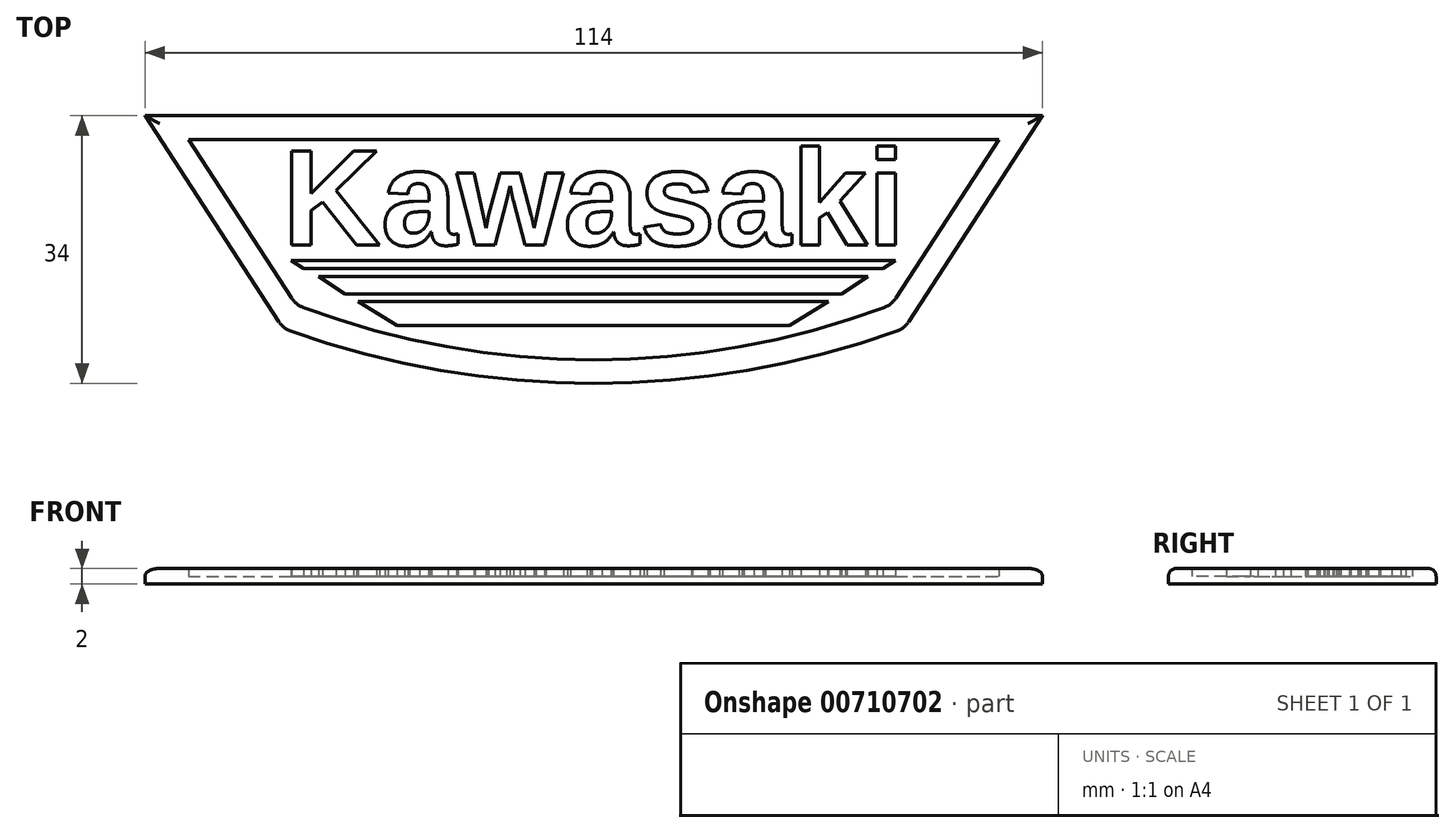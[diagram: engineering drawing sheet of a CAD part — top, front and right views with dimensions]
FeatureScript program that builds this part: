
annotation { "Feature Type Name" : "Feature", "Feature Type Description" : "" }
export const myFeature = defineFeature(function(context is Context, id is Id, definition is map)
    precondition{}
    {
        {
            var Q0;
            Q0=qCreatedBy(makeId("Top.planeOp"),FACE);
            var sketch = newSketch(context, id + "F0", { "sketchPlane" : qUnion([Q0])});
            skLineSegment(sketch, "E0.bottom", {"start": v(57, -17) * mm, "end": v(-57, -17) * mm});
            skLineSegment(sketch, "E0.top", {"start": v(57, 17) * mm, "end": v(-57, 17) * mm});
            skLineSegment(sketch, "E0.left", {"start": v(57, -17) * mm, "end": v(57, 17) * mm});
            skLineSegment(sketch, "E0.right", {"start": v(-57, -17) * mm, "end": v(-57, 17) * mm});
            skPoint(sketch, "E0.middle", {"position": v(0, 0) * mm});
            skLineSegment(sketch, "E1.top", {"start": v(57, -10) * mm, "end": v(-57, -10) * mm});
            skLineSegment(sketch, "E1.right", {"start": v(-57, 17) * mm, "end": v(-57, -10) * mm});
            skLineSegment(sketch, "E2", {"start": v(-57, 17) * mm, "end": v(-40.01, -9.15) * mm});
            skLineSegment(sketch, "E3", {"start": v(57, 17) * mm, "end": v(40.01, -9.15) * mm});
            skArc(sketch, "E4", {"start": v(-38.5, -10.35) * mm, "mid": v(0, -17) * mm, "end": v(38.5, -10.35) * mm});
            skLineSegment(sketch, "E5", {"start": v(-51.47, 14) * mm, "end": v(51.47, 14) * mm});
            skLineSegment(sketch, "E6", {"start": v(-51.47, 14) * mm, "end": v(-38.37, -6.18) * mm});
            skLineSegment(sketch, "E7", {"start": v(38.37, -6.18) * mm, "end": v(51.47, 14) * mm});
            skArc(sketch, "E8", {"start": v(-36.9, -7.35) * mm, "mid": v(0, -14) * mm, "end": v(36.9, -7.35) * mm});
            skPoint(sketch, "E9.visualSharp", {"position": v(-39.47, -10) * mm});
            skArc(sketch, "E9.filletArc", {"start": v(-40.01, -9.15) * mm, "mid": v(-39.36, -9.88) * mm, "end": v(-38.5, -10.35) * mm});
            skPoint(sketch, "E10.visualSharp", {"position": v(-37.84, -7) * mm});
            skArc(sketch, "E10.filletArc", {"start": v(-38.37, -6.18) * mm, "mid": v(-37.73, -6.88) * mm, "end": v(-36.9, -7.35) * mm});
            skPoint(sketch, "E11.visualSharp", {"position": v(37.84, -7) * mm});
            skArc(sketch, "E11.filletArc", {"start": v(36.9, -7.35) * mm, "mid": v(37.73, -6.88) * mm, "end": v(38.37, -6.18) * mm});
            skPoint(sketch, "E12.visualSharp", {"position": v(39.47, -10) * mm});
            skArc(sketch, "E12.filletArc", {"start": v(38.5, -10.35) * mm, "mid": v(39.36, -9.88) * mm, "end": v(40.01, -9.15) * mm});
            skSolve(sketch);
        }
        {
            var Q0;
            Q0=makeQuery(id+"F0.imprint","IMPRINT",FACE,{"disambiguationData":[TD([[makeQuery(id+"F0.imprint","IMPRINT",EDGE,{"derivedFrom":sQuery(id+"F0.wireOp",EDGE,"E5")}),-1.0]])]});
            var sketch = newSketch(context, id + "F1", { "sketchPlane" : qUnion([Q0])});
            skText(sketch, "E13", { "text": "Kawasaki", "fontName": "Arimo-Bold.ttf"});
            skLineSegment(sketch, "E14.bottom", {"start": v(-38.48, -1.42) * mm, "end": v(38.36, -1.42) * mm});
            skLineSegment(sketch, "E14.top", {"start": v(-38.48, -2.42) * mm, "end": v(38.36, -2.42) * mm});
            skLineSegment(sketch, "E14.left", {"start": v(-38.48, -1.42) * mm, "end": v(-38.48, -2.42) * mm});
            skLineSegment(sketch, "E14.right", {"start": v(38.36, -1.42) * mm, "end": v(38.36, -2.42) * mm});
            skLineSegment(sketch, "E15.bottom", {"start": v(-34.98, -3.42) * mm, "end": v(34.86, -3.42) * mm});
            skLineSegment(sketch, "E15.top", {"start": v(-34.98, -5.62) * mm, "end": v(34.86, -5.62) * mm});
            skLineSegment(sketch, "E15.left", {"start": v(-34.98, -3.42) * mm, "end": v(-34.98, -5.62) * mm});
            skLineSegment(sketch, "E15.right", {"start": v(34.86, -3.42) * mm, "end": v(34.86, -5.62) * mm});
            skLineSegment(sketch, "E16.bottom", {"start": v(-24.98, -6.62) * mm, "end": v(24.86, -6.62) * mm});
            skLineSegment(sketch, "E16.top", {"start": v(-24.98, -9.62) * mm, "end": v(24.86, -9.62) * mm});
            skLineSegment(sketch, "E16.left", {"start": v(-24.98, -6.62) * mm, "end": v(-24.98, -9.62) * mm});
            skLineSegment(sketch, "E16.right", {"start": v(24.86, -6.62) * mm, "end": v(24.86, -9.62) * mm});
            skLineSegment(sketch, "E17", {"start": v(38.36, -1.42) * mm, "end": v(24.86, -9.62) * mm, "construction": true});
            skLineSegment(sketch, "E18", {"start": v(38.36, -1.42) * mm, "end": v(36.7, -2.42) * mm, "construction": true});
            skLineSegment(sketch, "E19", {"start": v(36.7, -2.42) * mm, "end": v(38.36, -1.42) * mm, "construction": true});
            skLineSegment(sketch, "E20", {"start": v(38.36, -1.42) * mm, "end": v(36.7, -2.42) * mm});
            skLineSegment(sketch, "E21", {"start": v(34.86, -3.42) * mm, "end": v(31.44, -5.62) * mm});
            skLineSegment(sketch, "E22", {"start": v(24.86, -6.62) * mm, "end": v(29.8, -6.62) * mm});
            skLineSegment(sketch, "E23", {"start": v(29.8, -6.62) * mm, "end": v(24.86, -9.62) * mm});
            skLineSegment(sketch, "E24", {"start": v(-38.48, -1.42) * mm, "end": v(-24.98, -9.62) * mm, "construction": true});
            skLineSegment(sketch, "E25", {"start": v(-38.48, -1.42) * mm, "end": v(-36.83, -2.42) * mm});
            skLineSegment(sketch, "E26", {"start": v(-34.98, -3.42) * mm, "end": v(-31.56, -5.62) * mm});
            skLineSegment(sketch, "E27", {"start": v(-24.98, -6.62) * mm, "end": v(-29.92, -6.62) * mm});
            skLineSegment(sketch, "E28", {"start": v(-29.92, -6.62) * mm, "end": v(-24.98, -9.62) * mm});
            const initialGuessF1  = {"E13": [-0.03956, 0.00058, 1, 0, 0.0125]};
            skSetInitialGuess(sketch, initialGuessF1);
            skSolve(sketch);
        }
        {
            var Q0;
            Q0=makeQuery(id+"F0.imprint","IMPRINT",FACE,{"disambiguationData":[TD([[makeQuery(id+"F0.imprint","IMPRINT",EDGE,{"derivedFrom":sQuery(id+"F0.wireOp",EDGE,"E0.top")}),1.0]])]});
            var Q1;
            {var subQ0=sQuery(id+"F0.wireOp",EDGE,"E4");Q1=makeQuery(id+"F0.imprint","IMPRINT",FACE,{"disambiguationData":[TD([[makeQuery(id+"F0.imprint","IMPRINT",EDGE,{"derivedFrom":subQ0}),1.0]])]});}
            extrude(context, id + "F2", {"entities" : qUnion([Q0, Q1]), "depth" : 2 * mm, "offsetDistance" : 25 * mm});
        }
        {
            var Q0;
            Q0=makeQuery(id+"F0.imprint","IMPRINT",FACE,{"disambiguationData":[TD([[makeQuery(id+"F0.imprint","IMPRINT",EDGE,{"derivedFrom":sQuery(id+"F0.wireOp",EDGE,"E5")}),-1.0]])]});
            var Q1;
            {var subQ0=sQuery(id+"F0.wireOp",EDGE,"E8");var subQ1=sQuery(id+"F0.wireOp",EDGE,"E1.top");var subQ2=makeQuery(id+"F0.imprint","INTERSECT",VERTEX,{"disambiguationData":[OD(0.0)],"derivedFrom":[subQ1,subQ0]});Q1=makeQuery(id+"F0.imprint","IMPRINT",FACE,{"disambiguationData":[TD([[makeQuery(id+"F0.imprint","IMPRINT",EDGE,{"disambiguationData":[TD([[subQ2,-1.0]])],"derivedFrom":subQ1}),1.0]])]});}
            extrude(context, id + "F3", {"entities" : qUnion([Q0, Q1]), "operationType" : NewBodyOperationType.ADD, "depth" : 1 * mm, "offsetDistance" : 25 * mm});
        }
        {
            var Q0;
            Q0=makeQuery(id+"F1.imprint","IMPRINT",FACE,{"disambiguationData":[TD([[makeQuery(id+"F1.imprint","IMPRINT",EDGE,{"derivedFrom":sQuery(id+"F1.wireOp",EDGE,"E13.sketch_text.stroke-0")}),-1.0]])]});
            var Q1;
            Q1=makeQuery(id+"F1.imprint","IMPRINT",FACE,{"disambiguationData":[TD([[makeQuery(id+"F1.imprint","IMPRINT",EDGE,{"derivedFrom":sQuery(id+"F1.wireOp",EDGE,"E13.sketch_text.stroke-50")}),-1.0]])]});
            var Q2;
            Q2=makeQuery(id+"F1.imprint","IMPRINT",FACE,{"disambiguationData":[TD([[makeQuery(id+"F1.imprint","IMPRINT",EDGE,{"derivedFrom":sQuery(id+"F1.wireOp",EDGE,"E13.sketch_text.stroke-107")}),-1.0]])]});
            var Q3;
            Q3=makeQuery(id+"F1.imprint","IMPRINT",FACE,{"disambiguationData":[TD([[makeQuery(id+"F1.imprint","IMPRINT",EDGE,{"derivedFrom":sQuery(id+"F1.wireOp",EDGE,"E13.sketch_text.stroke-174")}),-1.0]])]});
            var Q4;
            Q4=makeQuery(id+"F1.imprint","IMPRINT",FACE,{"disambiguationData":[TD([[makeQuery(id+"F1.imprint","IMPRINT",EDGE,{"derivedFrom":sQuery(id+"F1.wireOp",EDGE,"E13.sketch_text.stroke-186")}),-1.0]])]});
            var Q5;
            Q5=makeQuery(id+"F1.imprint","IMPRINT",FACE,{"disambiguationData":[TD([[makeQuery(id+"F1.imprint","IMPRINT",EDGE,{"derivedFrom":sQuery(id+"F1.wireOp",EDGE,"E13.sketch_text.stroke-190")}),-1.0]])]});
            var Q6;
            Q6=makeQuery(id+"F1.imprint","IMPRINT",FACE,{"disambiguationData":[TD([[makeQuery(id+"F1.imprint","IMPRINT",EDGE,{"derivedFrom":sQuery(id+"F1.wireOp",EDGE,"E16.bottom")}),-1.0]])]});
            var Q7;
            Q7=makeQuery(id+"F1.imprint","IMPRINT",FACE,{"disambiguationData":[TD([[makeQuery(id+"F1.imprint","IMPRINT",EDGE,{"derivedFrom":sQuery(id+"F1.wireOp",EDGE,"E13.sketch_text.stroke-12")}),-1.0]])]});
            var Q8;
            Q8=makeQuery(id+"F1.imprint","IMPRINT",FACE,{"disambiguationData":[TD([[makeQuery(id+"F1.imprint","IMPRINT",EDGE,{"derivedFrom":sQuery(id+"F1.wireOp",EDGE,"E13.sketch_text.stroke-69")}),-1.0]])]});
            var Q9;
            Q9=makeQuery(id+"F1.imprint","IMPRINT",FACE,{"disambiguationData":[TD([[makeQuery(id+"F1.imprint","IMPRINT",EDGE,{"derivedFrom":sQuery(id+"F1.wireOp",EDGE,"E13.sketch_text.stroke-136")}),-1.0]])]});
            var Q10;
            Q10=makeQuery(id+"F1.imprint","IMPRINT",FACE,{"disambiguationData":[TD([[makeQuery(id+"F1.imprint","IMPRINT",EDGE,{"derivedFrom":sQuery(id+"F1.wireOp",EDGE,"E14.bottom")}),-1.0]])]});
            var Q11;
            Q11=makeQuery(id+"F1.imprint","IMPRINT",FACE,{"disambiguationData":[TD([[makeQuery(id+"F1.imprint","IMPRINT",EDGE,{"derivedFrom":sQuery(id+"F1.wireOp",EDGE,"E15.bottom")}),-1.0]])]});
            var Q12;
            Q12=makeQuery(id+"F1.imprint","IMPRINT",FACE,{"disambiguationData":[TD([[makeQuery(id+"F1.imprint","IMPRINT",EDGE,{"derivedFrom":sQuery(id+"F1.wireOp",EDGE,"E16.left")}),-1.0]])]});
            var Q13;
            Q13=makeQuery(id+"F1.imprint","IMPRINT",FACE,{"disambiguationData":[TD([[makeQuery(id+"F1.imprint","IMPRINT",EDGE,{"derivedFrom":sQuery(id+"F1.wireOp",EDGE,"E16.right")}),1.0]])]});
            extrude(context, id + "F4", {"entities" : qUnion([Q0, Q1, Q2, Q3, Q4, Q5, Q6, Q7, Q8, Q9, Q10, Q11, Q12, Q13]), "operationType" : NewBodyOperationType.ADD, "depth" : 2 * mm, "offsetDistance" : 25 * mm});
        }
        {
            var Q0;
            Q0=makeQuery(id+"F2.opExtrude","CAP_EDGE",EDGE,{"disambiguationData":[OSD([sQuery(id+"F0.wireOp",EDGE,"E4")])],"isStart":false});
            var Q1;
            Q1=makeQuery(id+"F2.opExtrude","CAP_EDGE",EDGE,{"disambiguationData":[OSD([sQuery(id+"F0.wireOp",EDGE,"E0.top")])],"isStart":false});
            fillet(context, id + "F5", {"entities" : qUnion([Q0, Q1]), "radius" : 1 * mm, "tangentPropagation" : true, "allowEdgeOverflow" : false});
        }
    });
